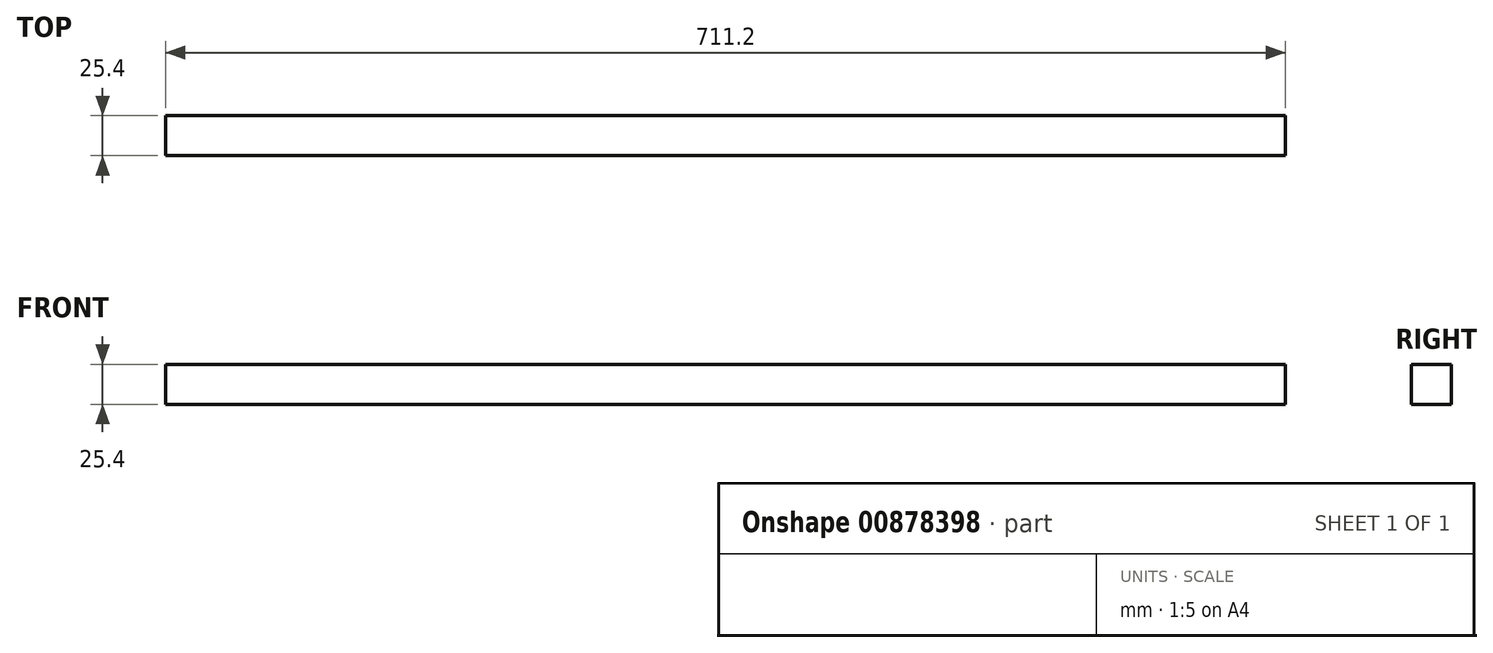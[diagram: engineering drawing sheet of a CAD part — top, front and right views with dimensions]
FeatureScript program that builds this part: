
annotation { "Feature Type Name" : "Feature", "Feature Type Description" : "" }
export const myFeature = defineFeature(function(context is Context, id is Id, definition is map)
    precondition{}
    {
        {
            var Q0;
            Q0=qCreatedBy(makeId("Top.planeOp"),FACE);
            var sketch = newSketch(context, id + "F0", { "sketchPlane" : qUnion([Q0])});
            skLineSegment(sketch, "E0.bottom", {"start": v(0, 0) * mm, "end": v(711.2, 0) * mm});
            skLineSegment(sketch, "E0.top", {"start": v(0, 25.4) * mm, "end": v(711.2, 25.4) * mm});
            skLineSegment(sketch, "E0.left", {"start": v(0, 0) * mm, "end": v(0, 25.4) * mm});
            skLineSegment(sketch, "E0.right", {"start": v(711.2, 0) * mm, "end": v(711.2, 25.4) * mm});
            skSolve(sketch);
        }
        {
            var Q0;
            Q0=makeQuery(id+"F0.imprint","IMPRINT",FACE,{"disambiguationData":[TD([[makeQuery(id+"F0.imprint","IMPRINT",EDGE,{"derivedFrom":sQuery(id+"F0.wireOp",EDGE,"E0.bottom")}),1.0]])]});
            extrude(context, id + "F1", {"entities" : qUnion([Q0]), "depth" : 25.4 * mm, "offsetDistance" : 25.4 * mm});
        }
    });
